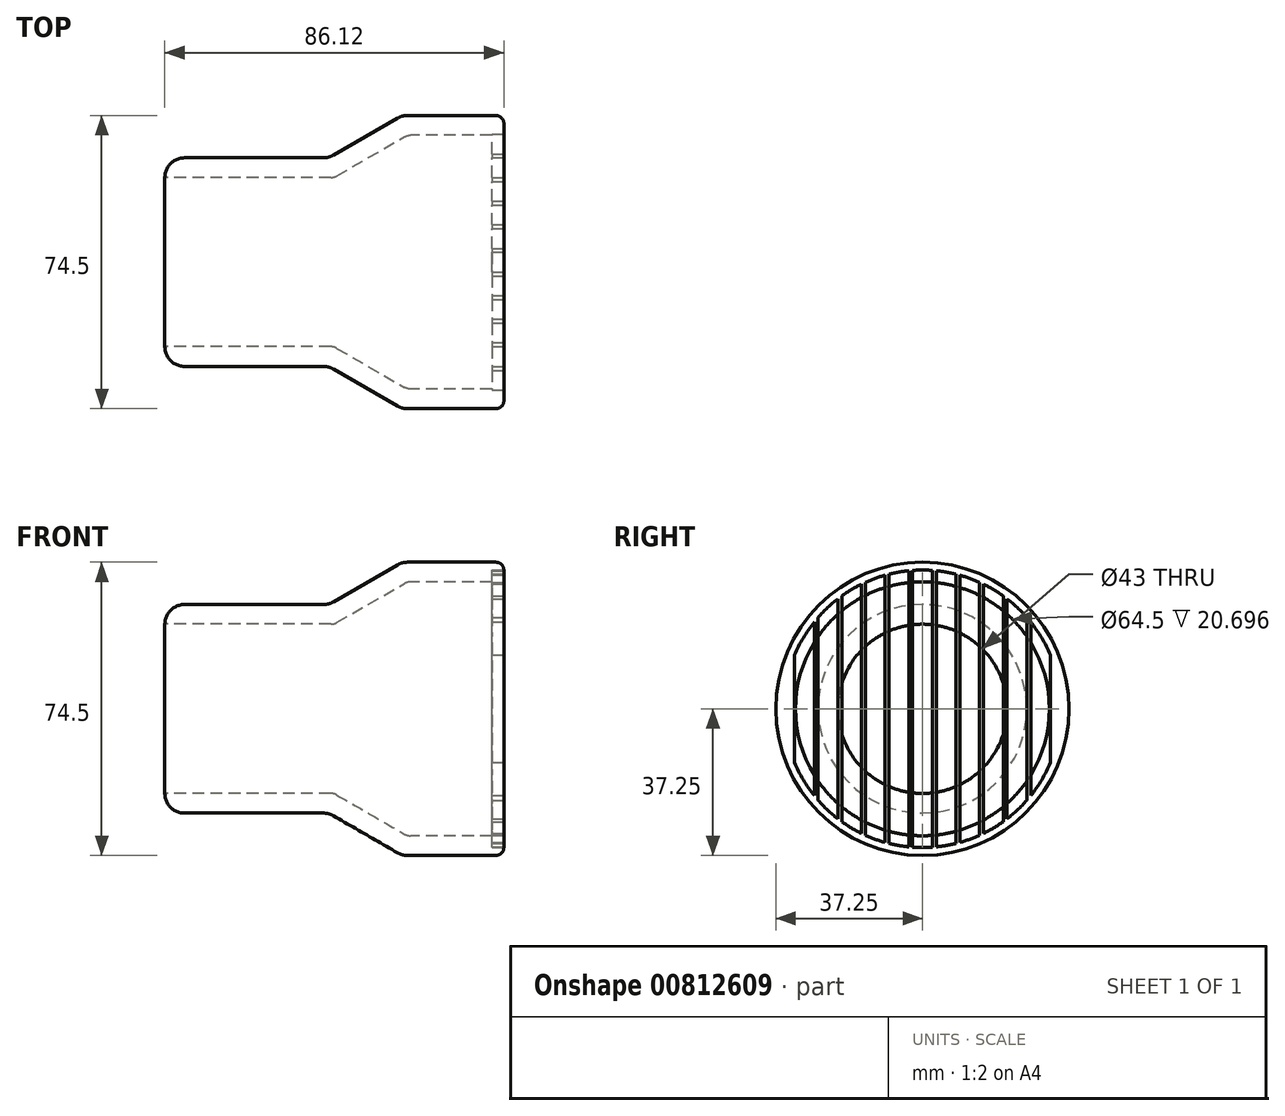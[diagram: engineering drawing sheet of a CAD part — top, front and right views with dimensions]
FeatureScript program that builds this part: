
annotation { "Feature Type Name" : "Feature", "Feature Type Description" : "" }
export const myFeature = defineFeature(function(context is Context, id is Id, definition is map)
    precondition{}
    {
        {
            var Q0;
            Q0=qCreatedBy(makeId("Top.planeOp"),FACE);
            var sketch = newSketch(context, id + "F0", { "sketchPlane" : qUnion([Q0])});
            skLineSegment(sketch, "E0", {"start": v(-43, 21.5) * mm, "end": v(0, 21.5) * mm});
            skLineSegment(sketch, "E1", {"start": v(0, 21.5) * mm, "end": v(18.62, 32.25) * mm});
            skLineSegment(sketch, "E2", {"start": v(18.62, 32.25) * mm, "end": v(40.12, 32.25) * mm});
            skLineSegment(sketch, "E3.0", {"start": v(17.28, 37.25) * mm, "end": v(40.12, 37.25) * mm});
            skLineSegment(sketch, "E3.1", {"start": v(-1.34, 26.5) * mm, "end": v(17.28, 37.25) * mm});
            skLineSegment(sketch, "E3.2", {"start": v(-43, 26.5) * mm, "end": v(-1.34, 26.5) * mm});
            skLineSegment(sketch, "E4", {"start": v(-43, 21.5) * mm, "end": v(-43, 26.5) * mm});
            skLineSegment(sketch, "E5", {"start": v(40.12, 37.25) * mm, "end": v(40.12, 32.25) * mm});
            skLineSegment(sketch, "E6", {"start": v(-63.57, 0) * mm, "end": v(46.05, 0) * mm});
            skSolve(sketch);
        }
        {
            var Q0;
            Q0 = qSketchRegion(id + "F0", true);
            var Q1;
            Q1=sQuery(id+"F0.wireOp",EDGE,"E6");
            revolve(context, id + "F1", {"surfaceOperationType" : NewSurfaceOperationType.NEW, "entities" : qUnion([Q0]), "axis" : qUnion([Q1]), "revolveType" : RevolveType.FULL});
        }
        {
            var Q0;
            Q0=makeQuery(id+"F1.opRevolve","SWEPT_FACE",FACE,{"disambiguationData":[OSD([sQuery(id+"F0.wireOp",EDGE,"E5")])]});
            var sketch = newSketch(context, id + "F2", { "sketchPlane" : qUnion([Q0])});
            skCircle(sketch, "E7.0", {"center": v(0, 0) * mm, "radius": 37.25 * mm});
            skSolve(sketch);
        }
        {
            var Q0;
            Q0 = qSketchRegion(id + "F2", true);
            extrude(context, id + "F3", {"entities" : qUnion([Q0]), "operationType" : NewBodyOperationType.ADD, "depth" : 3 * mm, "offsetDistance" : 25 * mm});
        }
        {
            var Q0;
            Q0=makeQuery(id+"F3.opExtrude","CAP_EDGE",EDGE,{"disambiguationData":[OSD([sQuery(id+"F2.wireOp",EDGE,"E7.0")])],"isStart":false});
            fillet(context, id + "F4", {"entities" : qUnion([Q0]), "radius" : 2 * mm, "tangentPropagation" : true, "allowEdgeOverflow" : false});
        }
        {
            var Q0;
            Q0=makeQuery(id+"F3.opExtrude","CAP_FACE",FACE,{"disambiguationData":[OSD([sQuery(id+"F2.wireOp",EDGE,"E7.0")])],"isStart":false});
            var sketch = newSketch(context, id + "F5", { "sketchPlane" : qUnion([Q0])});
            skLineSegment(sketch, "E8.bottom", {"start": v(-2.5, 42.44) * mm, "end": v(2.5, 42.44) * mm});
            skLineSegment(sketch, "E8.top", {"start": v(-2.5, -43.56) * mm, "end": v(2.5, -43.56) * mm});
            skLineSegment(sketch, "E8.left", {"start": v(-2.5, 42.44) * mm, "end": v(-2.5, -43.56) * mm});
            skLineSegment(sketch, "E8.right", {"start": v(2.5, 42.44) * mm, "end": v(2.5, -43.56) * mm});
            skLineSegment(sketch, "E9.1.0.0", {"start": v(3.5, -43.56) * mm, "end": v(8.5, -43.56) * mm});
            skLineSegment(sketch, "E9.1.0.1", {"start": v(8.5, 42.44) * mm, "end": v(8.5, -43.56) * mm});
            skLineSegment(sketch, "E9.1.0.2", {"start": v(3.5, 42.44) * mm, "end": v(3.5, -43.56) * mm});
            skLineSegment(sketch, "E9.1.0.3", {"start": v(3.5, 42.44) * mm, "end": v(8.5, 42.44) * mm});
            skLineSegment(sketch, "E9.2.0.0", {"start": v(9.5, -43.56) * mm, "end": v(14.5, -43.56) * mm});
            skLineSegment(sketch, "E9.2.0.1", {"start": v(14.5, 42.44) * mm, "end": v(14.5, -43.56) * mm});
            skLineSegment(sketch, "E9.2.0.2", {"start": v(9.5, 42.44) * mm, "end": v(9.5, -43.56) * mm});
            skLineSegment(sketch, "E9.2.0.3", {"start": v(9.5, 42.44) * mm, "end": v(14.5, 42.44) * mm});
            skLineSegment(sketch, "E9.3.0.0", {"start": v(15.5, -43.56) * mm, "end": v(20.5, -43.56) * mm});
            skLineSegment(sketch, "E9.3.0.1", {"start": v(20.5, 42.44) * mm, "end": v(20.5, -43.56) * mm});
            skLineSegment(sketch, "E9.3.0.2", {"start": v(15.5, 42.44) * mm, "end": v(15.5, -43.56) * mm});
            skLineSegment(sketch, "E9.3.0.3", {"start": v(15.5, 42.44) * mm, "end": v(20.5, 42.44) * mm});
            skLineSegment(sketch, "E9.4.0.0", {"start": v(21.5, -43.56) * mm, "end": v(26.5, -43.56) * mm});
            skLineSegment(sketch, "E9.4.0.1", {"start": v(26.5, 42.44) * mm, "end": v(26.5, -43.56) * mm});
            skLineSegment(sketch, "E9.4.0.2", {"start": v(21.5, 42.44) * mm, "end": v(21.5, -43.56) * mm});
            skLineSegment(sketch, "E9.4.0.3", {"start": v(21.5, 42.44) * mm, "end": v(26.5, 42.44) * mm});
            skLineSegment(sketch, "E9.5.0.0", {"start": v(27.5, -43.56) * mm, "end": v(32.5, -43.56) * mm});
            skLineSegment(sketch, "E9.5.0.1", {"start": v(32.5, 42.44) * mm, "end": v(32.5, -43.56) * mm});
            skLineSegment(sketch, "E9.5.0.2", {"start": v(27.5, 42.44) * mm, "end": v(27.5, -43.56) * mm});
            skLineSegment(sketch, "E9.5.0.3", {"start": v(27.5, 42.44) * mm, "end": v(32.5, 42.44) * mm});
            skLineSegment(sketch, "E9.6.0.0", {"start": v(33.5, -43.56) * mm, "end": v(38.5, -43.56) * mm});
            skLineSegment(sketch, "E9.6.0.1", {"start": v(38.5, 42.44) * mm, "end": v(38.5, -43.56) * mm});
            skLineSegment(sketch, "E9.6.0.2", {"start": v(33.5, 42.44) * mm, "end": v(33.5, -43.56) * mm});
            skLineSegment(sketch, "E9.6.0.3", {"start": v(33.5, 42.44) * mm, "end": v(38.5, 42.44) * mm});
            skLineSegment(sketch, "E9.7.0.0", {"start": v(39.5, -43.56) * mm, "end": v(44.5, -43.56) * mm});
            skLineSegment(sketch, "E9.7.0.1", {"start": v(44.5, 42.44) * mm, "end": v(44.5, -43.56) * mm});
            skLineSegment(sketch, "E9.7.0.2", {"start": v(39.5, 42.44) * mm, "end": v(39.5, -43.56) * mm});
            skLineSegment(sketch, "E9.7.0.3", {"start": v(39.5, 42.44) * mm, "end": v(44.5, 42.44) * mm});
            skLineSegment(sketch, "E9.8.0.0", {"start": v(45.5, -43.56) * mm, "end": v(50.5, -43.56) * mm});
            skLineSegment(sketch, "E9.8.0.1", {"start": v(50.5, 42.44) * mm, "end": v(50.5, -43.56) * mm});
            skLineSegment(sketch, "E9.8.0.2", {"start": v(45.5, 42.44) * mm, "end": v(45.5, -43.56) * mm});
            skLineSegment(sketch, "E9.8.0.3", {"start": v(45.5, 42.44) * mm, "end": v(50.5, 42.44) * mm});
            skLineSegment(sketch, "E9.direction1", {"start": v(-2.5, -43.56) * mm, "end": v(3.5, -43.56) * mm, "construction": true});
            skLineSegment(sketch, "E10.1.0.0", {"start": v(-3.5, 42.44) * mm, "end": v(-3.5, -43.56) * mm});
            skLineSegment(sketch, "E10.1.0.1", {"start": v(-8.5, -43.56) * mm, "end": v(-3.5, -43.56) * mm});
            skLineSegment(sketch, "E10.1.0.2", {"start": v(-8.5, 42.44) * mm, "end": v(-8.5, -43.56) * mm});
            skLineSegment(sketch, "E10.1.0.3", {"start": v(-8.5, 42.44) * mm, "end": v(-3.5, 42.44) * mm});
            skLineSegment(sketch, "E10.2.0.0", {"start": v(-9.5, 42.44) * mm, "end": v(-9.5, -43.56) * mm});
            skLineSegment(sketch, "E10.2.0.1", {"start": v(-14.5, -43.56) * mm, "end": v(-9.5, -43.56) * mm});
            skLineSegment(sketch, "E10.2.0.2", {"start": v(-14.5, 42.44) * mm, "end": v(-14.5, -43.56) * mm});
            skLineSegment(sketch, "E10.2.0.3", {"start": v(-14.5, 42.44) * mm, "end": v(-9.5, 42.44) * mm});
            skLineSegment(sketch, "E10.3.0.0", {"start": v(-15.5, 42.44) * mm, "end": v(-15.5, -43.56) * mm});
            skLineSegment(sketch, "E10.3.0.1", {"start": v(-20.5, -43.56) * mm, "end": v(-15.5, -43.56) * mm});
            skLineSegment(sketch, "E10.3.0.2", {"start": v(-20.5, 42.44) * mm, "end": v(-20.5, -43.56) * mm});
            skLineSegment(sketch, "E10.3.0.3", {"start": v(-20.5, 42.44) * mm, "end": v(-15.5, 42.44) * mm});
            skLineSegment(sketch, "E10.4.0.0", {"start": v(-21.5, 42.44) * mm, "end": v(-21.5, -43.56) * mm});
            skLineSegment(sketch, "E10.4.0.1", {"start": v(-26.5, -43.56) * mm, "end": v(-21.5, -43.56) * mm});
            skLineSegment(sketch, "E10.4.0.2", {"start": v(-26.5, 42.44) * mm, "end": v(-26.5, -43.56) * mm});
            skLineSegment(sketch, "E10.4.0.3", {"start": v(-26.5, 42.44) * mm, "end": v(-21.5, 42.44) * mm});
            skLineSegment(sketch, "E10.5.0.0", {"start": v(-27.5, 42.44) * mm, "end": v(-27.5, -43.56) * mm});
            skLineSegment(sketch, "E10.5.0.1", {"start": v(-32.5, -43.56) * mm, "end": v(-27.5, -43.56) * mm});
            skLineSegment(sketch, "E10.5.0.2", {"start": v(-32.5, 42.44) * mm, "end": v(-32.5, -43.56) * mm});
            skLineSegment(sketch, "E10.5.0.3", {"start": v(-32.5, 42.44) * mm, "end": v(-27.5, 42.44) * mm});
            skLineSegment(sketch, "E10.6.0.0", {"start": v(-33.5, 42.44) * mm, "end": v(-33.5, -43.56) * mm});
            skLineSegment(sketch, "E10.6.0.1", {"start": v(-38.5, -43.56) * mm, "end": v(-33.5, -43.56) * mm});
            skLineSegment(sketch, "E10.6.0.2", {"start": v(-38.5, 42.44) * mm, "end": v(-38.5, -43.56) * mm});
            skLineSegment(sketch, "E10.6.0.3", {"start": v(-38.5, 42.44) * mm, "end": v(-33.5, 42.44) * mm});
            skLineSegment(sketch, "E10.7.0.0", {"start": v(-39.5, 42.44) * mm, "end": v(-39.5, -43.56) * mm});
            skLineSegment(sketch, "E10.7.0.1", {"start": v(-44.5, -43.56) * mm, "end": v(-39.5, -43.56) * mm});
            skLineSegment(sketch, "E10.7.0.2", {"start": v(-44.5, 42.44) * mm, "end": v(-44.5, -43.56) * mm});
            skLineSegment(sketch, "E10.7.0.3", {"start": v(-44.5, 42.44) * mm, "end": v(-39.5, 42.44) * mm});
            skLineSegment(sketch, "E10.8.0.0", {"start": v(-45.5, 42.44) * mm, "end": v(-45.5, -43.56) * mm});
            skLineSegment(sketch, "E10.8.0.1", {"start": v(-50.5, -43.56) * mm, "end": v(-45.5, -43.56) * mm});
            skLineSegment(sketch, "E10.8.0.2", {"start": v(-50.5, 42.44) * mm, "end": v(-50.5, -43.56) * mm});
            skLineSegment(sketch, "E10.8.0.3", {"start": v(-50.5, 42.44) * mm, "end": v(-45.5, 42.44) * mm});
            skLineSegment(sketch, "E10.direction1", {"start": v(-2.5, -43.56) * mm, "end": v(-8.5, -43.56) * mm, "construction": true});
            skSolve(sketch);
        }
        {
            var Q0;
            {var subQ0=sQuery(id+"F5.wireOp",EDGE,"E10.5.0.0");var subQ1=makeQuery(id+"F3.opExtrude","CAP_EDGE",EDGE,{"disambiguationData":[OSD([sQuery(id+"F2.wireOp",EDGE,"E7.0")])],"isStart":false});var subQ2=makeQuery(id+"F5.imprint","INTERSECT",VERTEX,{"disambiguationData":[OD(0.0)],"derivedFrom":[subQ1,subQ0]});Q0=makeQuery(id+"F5.imprint","IMPRINT",FACE,{"disambiguationData":[TD([[makeQuery(id+"F5.imprint","IMPRINT",EDGE,{"disambiguationData":[TD([[subQ2,-1.0]])],"derivedFrom":subQ0}),-1.0]])]});}
            var Q1;
            {var subQ0=sQuery(id+"F5.wireOp",EDGE,"E10.4.0.0");var subQ1=makeQuery(id+"F3.opExtrude","CAP_EDGE",EDGE,{"disambiguationData":[OSD([sQuery(id+"F2.wireOp",EDGE,"E7.0")])],"isStart":false});var subQ2=makeQuery(id+"F5.imprint","INTERSECT",VERTEX,{"disambiguationData":[OD(0.0)],"derivedFrom":[subQ1,subQ0]});Q1=makeQuery(id+"F5.imprint","IMPRINT",FACE,{"disambiguationData":[TD([[makeQuery(id+"F5.imprint","IMPRINT",EDGE,{"disambiguationData":[TD([[subQ2,-1.0]])],"derivedFrom":subQ0}),-1.0]])]});}
            var Q2;
            {var subQ0=sQuery(id+"F5.wireOp",EDGE,"E10.3.0.0");var subQ1=makeQuery(id+"F3.opExtrude","CAP_EDGE",EDGE,{"disambiguationData":[OSD([sQuery(id+"F2.wireOp",EDGE,"E7.0")])],"isStart":false});var subQ2=makeQuery(id+"F5.imprint","INTERSECT",VERTEX,{"disambiguationData":[OD(0.0)],"derivedFrom":[subQ1,subQ0]});Q2=makeQuery(id+"F5.imprint","IMPRINT",FACE,{"disambiguationData":[TD([[makeQuery(id+"F5.imprint","IMPRINT",EDGE,{"disambiguationData":[TD([[subQ2,-1.0]])],"derivedFrom":subQ0}),-1.0]])]});}
            var Q3;
            {var subQ0=sQuery(id+"F5.wireOp",EDGE,"E10.2.0.0");var subQ1=makeQuery(id+"F3.opExtrude","CAP_EDGE",EDGE,{"disambiguationData":[OSD([sQuery(id+"F2.wireOp",EDGE,"E7.0")])],"isStart":false});var subQ2=makeQuery(id+"F5.imprint","INTERSECT",VERTEX,{"disambiguationData":[OD(0.0)],"derivedFrom":[subQ1,subQ0]});Q3=makeQuery(id+"F5.imprint","IMPRINT",FACE,{"disambiguationData":[TD([[makeQuery(id+"F5.imprint","IMPRINT",EDGE,{"disambiguationData":[TD([[subQ2,-1.0]])],"derivedFrom":subQ0}),-1.0]])]});}
            var Q4;
            {var subQ0=sQuery(id+"F5.wireOp",EDGE,"E10.1.0.0");var subQ1=makeQuery(id+"F3.opExtrude","CAP_EDGE",EDGE,{"disambiguationData":[OSD([sQuery(id+"F2.wireOp",EDGE,"E7.0")])],"isStart":false});var subQ2=makeQuery(id+"F5.imprint","INTERSECT",VERTEX,{"disambiguationData":[OD(0.0)],"derivedFrom":[subQ1,subQ0]});Q4=makeQuery(id+"F5.imprint","IMPRINT",FACE,{"disambiguationData":[TD([[makeQuery(id+"F5.imprint","IMPRINT",EDGE,{"disambiguationData":[TD([[subQ2,-1.0]])],"derivedFrom":subQ0}),-1.0]])]});}
            var Q5;
            {var subQ0=sQuery(id+"F5.wireOp",EDGE,"E8.left");var subQ1=makeQuery(id+"F3.opExtrude","CAP_EDGE",EDGE,{"disambiguationData":[OSD([sQuery(id+"F2.wireOp",EDGE,"E7.0")])],"isStart":false});var subQ2=makeQuery(id+"F5.imprint","INTERSECT",VERTEX,{"disambiguationData":[OD(0.0)],"derivedFrom":[subQ1,subQ0]});Q5=makeQuery(id+"F5.imprint","IMPRINT",FACE,{"disambiguationData":[TD([[makeQuery(id+"F5.imprint","IMPRINT",EDGE,{"disambiguationData":[TD([[subQ2,-1.0]])],"derivedFrom":subQ0}),1.0]])]});}
            var Q6;
            {var subQ0=sQuery(id+"F5.wireOp",EDGE,"E9.1.0.1");var subQ1=makeQuery(id+"F3.opExtrude","CAP_EDGE",EDGE,{"disambiguationData":[OSD([sQuery(id+"F2.wireOp",EDGE,"E7.0")])],"isStart":false});var subQ2=makeQuery(id+"F5.imprint","INTERSECT",VERTEX,{"disambiguationData":[OD(0.0)],"derivedFrom":[subQ1,subQ0]});Q6=makeQuery(id+"F5.imprint","IMPRINT",FACE,{"disambiguationData":[TD([[makeQuery(id+"F5.imprint","IMPRINT",EDGE,{"disambiguationData":[TD([[subQ2,-1.0]])],"derivedFrom":subQ0}),-1.0]])]});}
            var Q7;
            {var subQ0=sQuery(id+"F5.wireOp",EDGE,"E9.2.0.1");var subQ1=makeQuery(id+"F3.opExtrude","CAP_EDGE",EDGE,{"disambiguationData":[OSD([sQuery(id+"F2.wireOp",EDGE,"E7.0")])],"isStart":false});var subQ2=makeQuery(id+"F5.imprint","INTERSECT",VERTEX,{"disambiguationData":[OD(0.0)],"derivedFrom":[subQ1,subQ0]});Q7=makeQuery(id+"F5.imprint","IMPRINT",FACE,{"disambiguationData":[TD([[makeQuery(id+"F5.imprint","IMPRINT",EDGE,{"disambiguationData":[TD([[subQ2,-1.0]])],"derivedFrom":subQ0}),-1.0]])]});}
            var Q8;
            {var subQ0=sQuery(id+"F5.wireOp",EDGE,"E9.3.0.1");var subQ1=makeQuery(id+"F3.opExtrude","CAP_EDGE",EDGE,{"disambiguationData":[OSD([sQuery(id+"F2.wireOp",EDGE,"E7.0")])],"isStart":false});var subQ2=makeQuery(id+"F5.imprint","INTERSECT",VERTEX,{"disambiguationData":[OD(0.0)],"derivedFrom":[subQ1,subQ0]});Q8=makeQuery(id+"F5.imprint","IMPRINT",FACE,{"disambiguationData":[TD([[makeQuery(id+"F5.imprint","IMPRINT",EDGE,{"disambiguationData":[TD([[subQ2,-1.0]])],"derivedFrom":subQ0}),-1.0]])]});}
            var Q9;
            {var subQ0=sQuery(id+"F5.wireOp",EDGE,"E9.4.0.1");var subQ1=makeQuery(id+"F3.opExtrude","CAP_EDGE",EDGE,{"disambiguationData":[OSD([sQuery(id+"F2.wireOp",EDGE,"E7.0")])],"isStart":false});var subQ2=makeQuery(id+"F5.imprint","INTERSECT",VERTEX,{"disambiguationData":[OD(0.0)],"derivedFrom":[subQ1,subQ0]});Q9=makeQuery(id+"F5.imprint","IMPRINT",FACE,{"disambiguationData":[TD([[makeQuery(id+"F5.imprint","IMPRINT",EDGE,{"disambiguationData":[TD([[subQ2,-1.0]])],"derivedFrom":subQ0}),-1.0]])]});}
            var Q10;
            {var subQ0=sQuery(id+"F5.wireOp",EDGE,"E9.5.0.1");var subQ1=makeQuery(id+"F3.opExtrude","CAP_EDGE",EDGE,{"disambiguationData":[OSD([sQuery(id+"F2.wireOp",EDGE,"E7.0")])],"isStart":false});var subQ2=makeQuery(id+"F5.imprint","INTERSECT",VERTEX,{"disambiguationData":[OD(0.0)],"derivedFrom":[subQ1,subQ0]});Q10=makeQuery(id+"F5.imprint","IMPRINT",FACE,{"disambiguationData":[TD([[makeQuery(id+"F5.imprint","IMPRINT",EDGE,{"disambiguationData":[TD([[subQ2,-1.0]])],"derivedFrom":subQ0}),-1.0]])]});}
            var Q11;
            Q11=makeQuery(id+"F3.opExtrude","CAP_FACE",FACE,{"disambiguationData":[OSD([sQuery(id+"F2.wireOp",EDGE,"E7.0")])],"isStart":true});
            extrude(context, id + "F6", {"entities" : qUnion([Q0, Q1, Q2, Q3, Q4, Q5, Q6, Q7, Q8, Q9, Q10]), "operationType" : NewBodyOperationType.REMOVE, "endBound" : BoundingType.UP_TO_SURFACE, "oppositeDirection" : true, "depth" : 25 * mm, "endBoundEntityFace" : qUnion([Q11]), "offsetDistance" : 25 * mm});
        }
        {
            var Q0;
            Q0=makeQuery(id+"F1.opRevolve","SWEPT_EDGE",EDGE,{"disambiguationData":[OSD([sQuery(id+"F0.wireOp",EDGE,"E3.2"),sQuery(id+"F0.wireOp",EDGE,"E4")])]});
            var Q1;
            Q1=makeQuery(id+"F1.opRevolve","SWEPT_EDGE",EDGE,{"disambiguationData":[OSD([sQuery(id+"F0.wireOp",EDGE,"E3.1"),sQuery(id+"F0.wireOp",EDGE,"E3.2")])]});
            var Q2;
            Q2=makeQuery(id+"F1.opRevolve","SWEPT_EDGE",EDGE,{"disambiguationData":[OSD([sQuery(id+"F0.wireOp",EDGE,"E3.0"),sQuery(id+"F0.wireOp",EDGE,"E3.1")])]});
            fillet(context, id + "F7", {"entities" : qUnion([Q0, Q1, Q2]), "radius" : 5 * mm, "tangentPropagation" : true, "allowEdgeOverflow" : false});
        }
        {
            var Q0;
            Q0=makeQuery(id+"F1.opRevolve","SWEPT_EDGE",EDGE,{"disambiguationData":[OSD([sQuery(id+"F0.wireOp",EDGE,"E1"),sQuery(id+"F0.wireOp",EDGE,"E2")])]});
            var Q1;
            Q1=makeQuery(id+"F1.opRevolve","SWEPT_EDGE",EDGE,{"disambiguationData":[OSD([sQuery(id+"F0.wireOp",EDGE,"E0"),sQuery(id+"F0.wireOp",EDGE,"E1")])]});
            fillet(context, id + "F8", {"entities" : qUnion([Q0, Q1]), "radius" : 3 * mm, "tangentPropagation" : true, "allowEdgeOverflow" : false});
        }
    });
